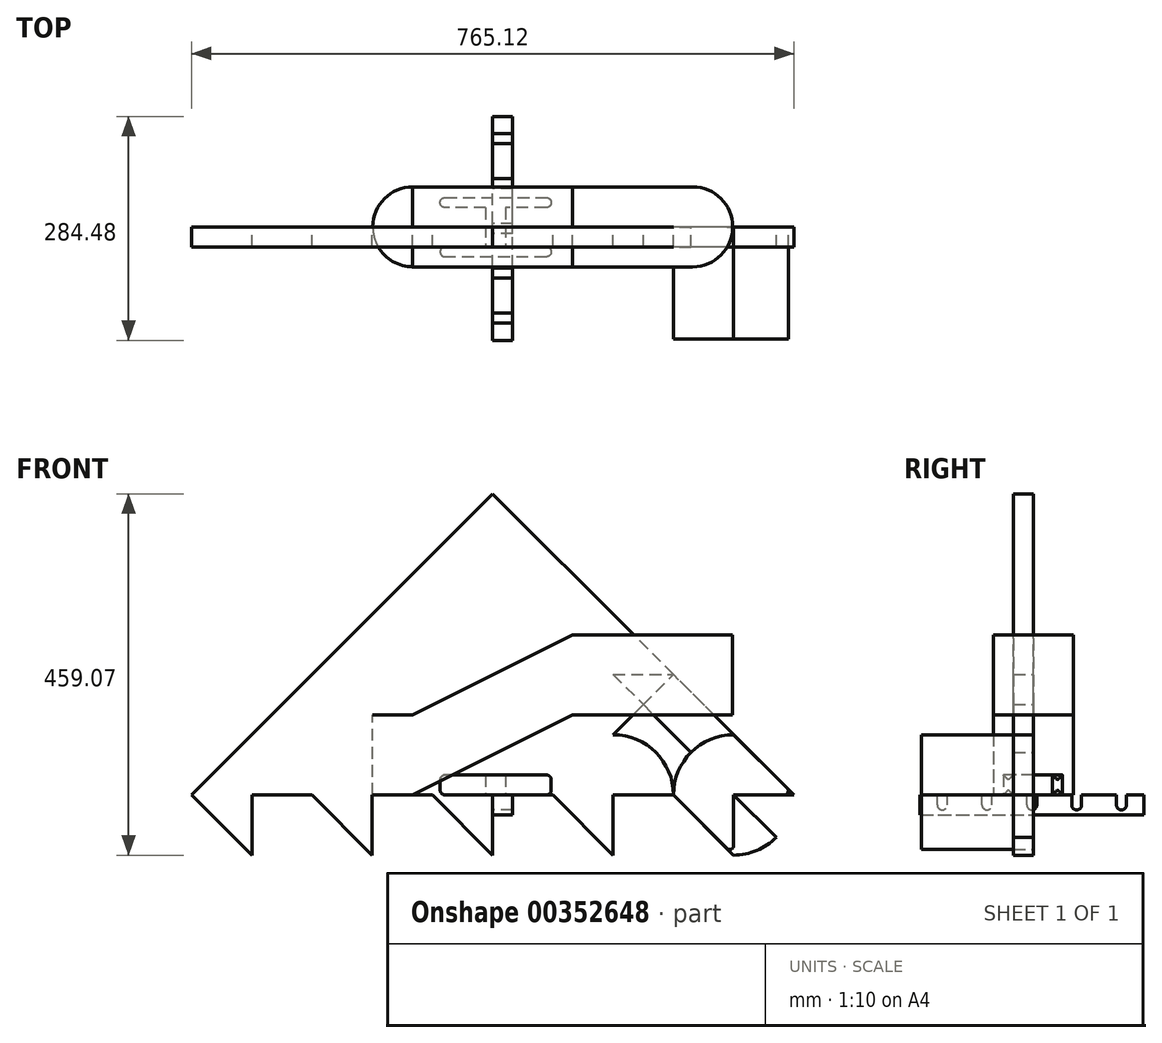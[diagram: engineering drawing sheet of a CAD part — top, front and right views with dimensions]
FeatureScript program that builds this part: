
annotation { "Feature Type Name" : "Feature", "Feature Type Description" : "" }
export const myFeature = defineFeature(function(context is Context, id is Id, definition is map)
    precondition{}
    {
        {
            var Q0;
            Q0=qCreatedBy(makeId("Front.planeOp"),FACE);
            var sketch = newSketch(context, id + "F0", { "sketchPlane" : qUnion([Q0])});
            skPoint(sketch, "E0", {"position": v(-101.6, 0) * mm});
            skPoint(sketch, "E1", {"position": v(101.6, 101.6) * mm});
            skLineSegment(sketch, "E2", {"start": v(-101.6, 0) * mm, "end": v(101.6, 0) * mm});
            skLineSegment(sketch, "E3", {"start": v(101.6, 0) * mm, "end": v(101.6, 101.6) * mm});
            skLineSegment(sketch, "E4", {"start": v(101.6, 101.6) * mm, "end": v(-101.6, 101.6) * mm});
            skLineSegment(sketch, "E5", {"start": v(-101.6, 101.6) * mm, "end": v(-101.6, 0) * mm});
            skLineSegment(sketch, "E6", {"start": v(-101.6, 203.2) * mm, "end": v(-101.6, 101.6) * mm});
            skLineSegment(sketch, "E7", {"start": v(101.6, 203.2) * mm, "end": v(101.6, 101.6) * mm});
            skLineSegment(sketch, "E8", {"start": v(-101.6, 203.2) * mm, "end": v(-101.6, 203.2) * mm});
            skLineSegment(sketch, "E9", {"start": v(101.6, 203.2) * mm, "end": v(101.6, 203.2) * mm});
            skLineSegment(sketch, "E10", {"start": v(101.6, 152.4) * mm, "end": v(-101.6, 152.4) * mm});
            skLineSegment(sketch, "E11", {"start": v(101.6, 50.8) * mm, "end": v(-101.6, 50.8) * mm});
            skLineSegment(sketch, "E12", {"start": v(101.6, 203.2) * mm, "end": v(-101.6, 203.2) * mm});
            skLineSegment(sketch, "E13", {"start": v(0, 203.2) * mm, "end": v(0, 0) * mm});
            skLineSegment(sketch, "E14", {"start": v(101.6, 203.2) * mm, "end": v(-101.6, 101.6) * mm});
            skLineSegment(sketch, "E15", {"start": v(101.6, 101.6) * mm, "end": v(-101.6, 0) * mm});
            skLineSegment(sketch, "E16.0", {"start": v(203.2, 0) * mm, "end": v(203.2, 101.6) * mm});
            skLineSegment(sketch, "E16.1", {"start": v(203.2, 203.2) * mm, "end": v(203.2, 101.6) * mm});
            skLineSegment(sketch, "E17.0", {"start": v(-203.2, 101.6) * mm, "end": v(-203.2, 0) * mm});
            skLineSegment(sketch, "E17.1", {"start": v(-203.2, 203.2) * mm, "end": v(-203.2, 101.6) * mm});
            skLineSegment(sketch, "E18", {"start": v(101.6, 203.2) * mm, "end": v(203.2, 203.2) * mm});
            skLineSegment(sketch, "E19", {"start": v(-101.6, 203.2) * mm, "end": v(-203.2, 203.2) * mm});
            skLineSegment(sketch, "E20", {"start": v(-203.2, 0) * mm, "end": v(-101.6, 0) * mm});
            skLineSegment(sketch, "E21", {"start": v(101.6, 0) * mm, "end": v(203.2, 0) * mm});
            skLineSegment(sketch, "E22", {"start": v(101.6, 101.6) * mm, "end": v(203.2, 101.6) * mm});
            skLineSegment(sketch, "E23", {"start": v(-101.6, 101.6) * mm, "end": v(-203.2, 101.6) * mm});
            skLineSegment(sketch, "E24", {"start": v(152.4, 203.2) * mm, "end": v(152.4, 101.6) * mm});
            skLineSegment(sketch, "E25", {"start": v(-152.4, 101.6) * mm, "end": v(-152.4, 0) * mm});
            skLineSegment(sketch, "E26.MirrorCS", {"start": v(254, 203.2) * mm, "end": v(254, 101.6) * mm});
            skLineSegment(sketch, "E27.MirrorCS", {"start": v(304.8, 203.2) * mm, "end": v(304.8, 101.6) * mm});
            skLineSegment(sketch, "E28", {"start": v(203.2, 203.2) * mm, "end": v(304.8, 203.2) * mm});
            skLineSegment(sketch, "E29", {"start": v(304.8, 101.6) * mm, "end": v(203.2, 101.6) * mm});
            skLineSegment(sketch, "E30.bottom", {"start": v(-152.4, 101.6) * mm, "end": v(-101.6, 101.6) * mm});
            skLineSegment(sketch, "E30.top", {"start": v(-152.4, 0) * mm, "end": v(-101.6, 0) * mm});
            skLineSegment(sketch, "E31", {"start": v(-108.75, 101.6) * mm, "end": v(-108.75, 0) * mm});
            skSolve(sketch);
        }
        {
            var Q0;
            {var subQ1=sQuery(id+"F0.wireOp",EDGE,"E7");var subQ3=sQuery(id+"F0.wireOp",EDGE,"E10");var subQ4=makeQuery(id+"F0.imprint","INTERSECT",VERTEX,{"derivedFrom":[subQ1,subQ3]});Q0=makeQuery(id+"F0.imprint","IMPRINT",FACE,{"disambiguationData":[TD([[makeQuery(id+"F0.imprint","IMPRINT",EDGE,{"disambiguationData":[TD([[subQ4,-1.0]])],"derivedFrom":subQ3}),-1.0]])]});}
            var Q1;
            {var subQ0=sQuery(id+"F0.wireOp",EDGE,"E7");var subQ5=sQuery(id+"F0.wireOp",EDGE,"E10");var subQ7=makeQuery(id+"F0.imprint","INTERSECT",VERTEX,{"derivedFrom":[subQ0,subQ5]});Q1=makeQuery(id+"F0.imprint","IMPRINT",FACE,{"disambiguationData":[TD([[makeQuery(id+"F0.imprint","IMPRINT",EDGE,{"disambiguationData":[TD([[subQ7,-1.0]])],"derivedFrom":subQ5}),1.0]])]});}
            var Q2;
            {var subQ1=sQuery(id+"F0.wireOp",EDGE,"E4");var subQ3=sQuery(id+"F0.wireOp",EDGE,"E13");var subQ4=makeQuery(id+"F0.imprint","INTERSECT",VERTEX,{"derivedFrom":[subQ1,subQ3]});Q2=makeQuery(id+"F0.imprint","IMPRINT",FACE,{"disambiguationData":[TD([[makeQuery(id+"F0.imprint","IMPRINT",EDGE,{"disambiguationData":[TD([[subQ4,1.0]])],"derivedFrom":subQ3}),-1.0]])]});}
            var Q3;
            {var subQ0=sQuery(id+"F0.wireOp",EDGE,"E5");var subQ5=sQuery(id+"F0.wireOp",EDGE,"E11");var subQ6=makeQuery(id+"F0.imprint","INTERSECT",VERTEX,{"derivedFrom":[subQ0,subQ5]});Q3=makeQuery(id+"F0.imprint","IMPRINT",FACE,{"disambiguationData":[TD([[makeQuery(id+"F0.imprint","IMPRINT",EDGE,{"disambiguationData":[TD([[subQ6,1.0]])],"derivedFrom":subQ5}),-1.0]])]});}
            var Q4;
            {var subQ1=sQuery(id+"F0.wireOp",EDGE,"E4");var subQ3=sQuery(id+"F0.wireOp",EDGE,"E13");var subQ4=makeQuery(id+"F0.imprint","INTERSECT",VERTEX,{"derivedFrom":[subQ1,subQ3]});Q4=makeQuery(id+"F0.imprint","IMPRINT",FACE,{"disambiguationData":[TD([[makeQuery(id+"F0.imprint","IMPRINT",EDGE,{"disambiguationData":[TD([[subQ4,-1.0]])],"derivedFrom":subQ3}),1.0]])]});}
            var Q5;
            {var subQ1=sQuery(id+"F0.wireOp",EDGE,"E5");var subQ3=sQuery(id+"F0.wireOp",EDGE,"E11");var subQ4=makeQuery(id+"F0.imprint","INTERSECT",VERTEX,{"derivedFrom":[subQ1,subQ3]});Q5=makeQuery(id+"F0.imprint","IMPRINT",FACE,{"disambiguationData":[TD([[makeQuery(id+"F0.imprint","IMPRINT",EDGE,{"disambiguationData":[TD([[subQ4,1.0]])],"derivedFrom":subQ3}),1.0]])]});}
            var Q6;
            {var subQ3=sQuery(id+"F0.wireOp",EDGE,"E24");Q6=makeQuery(id+"F0.imprint","IMPRINT",FACE,{"disambiguationData":[TD([[makeQuery(id+"F0.imprint","IMPRINT",EDGE,{"derivedFrom":subQ3}),-1.0]])]});}
            var Q7;
            {var subQ0=sQuery(id+"F0.wireOp",EDGE,"E16.1");Q7=makeQuery(id+"F0.imprint","IMPRINT",FACE,{"disambiguationData":[TD([[makeQuery(id+"F0.imprint","IMPRINT",EDGE,{"derivedFrom":subQ0}),-1.0]])]});}
            var Q8;
            {var subQ0=sQuery(id+"F0.wireOp",EDGE,"E16.1");Q8=makeQuery(id+"F0.imprint","IMPRINT",FACE,{"disambiguationData":[TD([[makeQuery(id+"F0.imprint","IMPRINT",EDGE,{"derivedFrom":subQ0}),1.0]])]});}
            extrude(context, id + "F1", {"entities" : qUnion([Q0, Q1, Q2, Q3, Q4, Q5, Q6, Q7, Q8]), "endBound" : BoundingType.SYMMETRIC, "depth" : 101.6 * mm});
        }
        {
            var Q0;
            {var subQ0=sQuery(id+"F0.wireOp",EDGE,"E26.MirrorCS");Q0=makeQuery(id+"F0.imprint","IMPRINT",FACE,{"disambiguationData":[TD([[makeQuery(id+"F0.imprint","IMPRINT",EDGE,{"derivedFrom":subQ0}),1.0]])]});}
            var Q1;
            Q1=sQuery(id+"F0.wireOp",EDGE,"E26.MirrorCS");
            revolve(context, id + "F2", {"operationType" : NewBodyOperationType.ADD, "entities" : qUnion([Q0]), "axis" : qUnion([Q1]), "revolveType" : RevolveType.SYMMETRIC, "angle" : 180 * degree});
        }
        {
            var Q0;
            {var subQ6=sQuery(id+"F0.wireOp",EDGE,"E31");Q0=makeQuery(id+"F0.imprint","IMPRINT",FACE,{"disambiguationData":[TD([[makeQuery(id+"F0.imprint","IMPRINT",EDGE,{"derivedFrom":subQ6}),1.0]])]});}
            extrude(context, id + "F3", {"entities" : qUnion([Q0]), "operationType" : NewBodyOperationType.ADD, "depth" : 2.3 * mm});
        }
        {
            var Q0;
            {var subQ0=sQuery(id+"F0.wireOp",EDGE,"E25");Q0=makeQuery(id+"F0.imprint","IMPRINT",FACE,{"disambiguationData":[TD([[makeQuery(id+"F0.imprint","IMPRINT",EDGE,{"derivedFrom":subQ0}),1.0]])]});}
            var Q1;
            {var subQ6=sQuery(id+"F0.wireOp",EDGE,"E31");Q1=makeQuery(id+"F0.imprint","IMPRINT",FACE,{"disambiguationData":[TD([[makeQuery(id+"F0.imprint","IMPRINT",EDGE,{"derivedFrom":subQ6}),1.0]])]});}
            var Q2;
            Q2=makeQuery(id+"F3.opExtrude","CAP_EDGE",EDGE,{"disambiguationData":[OSD([sQuery(id+"F0.wireOp",EDGE,"E5")])],"isStart":true});
            revolve(context, id + "F4", {"operationType" : NewBodyOperationType.ADD, "entities" : qUnion([Q0, Q1]), "axis" : qUnion([Q2]), "revolveType" : RevolveType.SYMMETRIC, "angle" : 180 * degree});
        }
        {
            var Q0;
            Q0=qCreatedBy(makeId("Right.planeOp"),FACE);
            var sketch = newSketch(context, id + "F5", { "sketchPlane" : qUnion([Q0])});
            skLineSegment(sketch, "E32.bottom", {"start": v(-144.13, 0) * mm, "end": v(140.35, 0) * mm});
            skLineSegment(sketch, "E32.top", {"start": v(-144.13, -25.4) * mm, "end": v(140.35, -25.4) * mm});
            skLineSegment(sketch, "E32.left", {"start": v(-144.13, 0) * mm, "end": v(-144.13, -25.4) * mm});
            skLineSegment(sketch, "E32.right", {"start": v(140.35, 0) * mm, "end": v(140.35, -25.4) * mm});
            skLineSegment(sketch, "E33", {"start": v(-144.13, -12.7) * mm, "end": v(140.35, -12.7) * mm});
            skLineSegment(sketch, "E34.0", {"start": v(-144.13, -6.35) * mm, "end": v(140.35, -6.35) * mm});
            skLineSegment(sketch, "E35.0", {"start": v(-87.23, 0) * mm, "end": v(-87.23, -25.4) * mm});
            skLineSegment(sketch, "E36.0", {"start": v(-30.34, 0) * mm, "end": v(-30.34, -25.4) * mm});
            skLineSegment(sketch, "E37.0", {"start": v(26.56, 0) * mm, "end": v(26.56, -25.4) * mm});
            skLineSegment(sketch, "E38.0", {"start": v(83.45, 0) * mm, "end": v(83.45, -25.4) * mm});
            skLineSegment(sketch, "E39.0", {"start": v(-115.68, 0) * mm, "end": v(-115.68, -25.4) * mm});
            skLineSegment(sketch, "E40.0", {"start": v(-58.79, 0) * mm, "end": v(-58.79, -25.4) * mm});
            skLineSegment(sketch, "E41.0", {"start": v(-1.89, 0) * mm, "end": v(-1.89, -25.4) * mm});
            skLineSegment(sketch, "E42.0", {"start": v(55, 0) * mm, "end": v(55, -25.4) * mm});
            skLineSegment(sketch, "E43.0", {"start": v(111.9, 0) * mm, "end": v(111.9, -25.4) * mm});
            skCircle(sketch, "E44", {"center": v(-115.68, -12.7) * mm, "radius": 6.35 * mm});
            skCircle(sketch, "E45", {"center": v(-58.79, -12.7) * mm, "radius": 6.35 * mm});
            skCircle(sketch, "E46", {"center": v(-1.89, -12.7) * mm, "radius": 6.35 * mm});
            skCircle(sketch, "E47", {"center": v(55, -12.7) * mm, "radius": 6.35 * mm});
            skCircle(sketch, "E48", {"center": v(111.9, -12.7) * mm, "radius": 6.35 * mm});
            skLineSegment(sketch, "E49", {"start": v(-109.33, -12.7) * mm, "end": v(-109.33, 0) * mm});
            skLineSegment(sketch, "E50", {"start": v(-122.03, -12.7) * mm, "end": v(-122.03, 0) * mm});
            skLineSegment(sketch, "E51", {"start": v(-65.14, -12.7) * mm, "end": v(-65.14, 0) * mm});
            skLineSegment(sketch, "E52", {"start": v(-52.44, -12.7) * mm, "end": v(-52.44, 0) * mm});
            skLineSegment(sketch, "E53", {"start": v(-8.24, -12.7) * mm, "end": v(-8.24, 0) * mm});
            skLineSegment(sketch, "E54", {"start": v(4.46, -12.7) * mm, "end": v(4.46, 0) * mm});
            skLineSegment(sketch, "E55", {"start": v(61.36, -12.7) * mm, "end": v(61.36, 0) * mm});
            skLineSegment(sketch, "E56", {"start": v(48.66, -12.7) * mm, "end": v(48.66, 0) * mm});
            skLineSegment(sketch, "E57", {"start": v(118.25, -12.7) * mm, "end": v(118.25, 0) * mm});
            skLineSegment(sketch, "E58", {"start": v(105.55, -12.7) * mm, "end": v(105.55, 0) * mm});
            skSolve(sketch);
        }
        {
            var Q0;
            {var subQ0=sQuery(id+"F5.wireOp",EDGE,"E32.left");var subQ1=sQuery(id+"F5.wireOp",EDGE,"E32.bottom");var subQ2=makeQuery(id+"F5.imprint","INTERSECT",VERTEX,{"derivedFrom":[subQ1,subQ0]});Q0=makeQuery(id+"F5.imprint","IMPRINT",FACE,{"disambiguationData":[TD([[makeQuery(id+"F5.imprint","IMPRINT",EDGE,{"disambiguationData":[TD([[subQ2,-1.0]])],"derivedFrom":subQ1}),-1.0]])]});}
            var Q1;
            {var subQ0=sQuery(id+"F5.wireOp",EDGE,"E32.right");var subQ1=sQuery(id+"F5.wireOp",EDGE,"E32.bottom");var subQ2=makeQuery(id+"F5.imprint","INTERSECT",VERTEX,{"derivedFrom":[subQ1,subQ0]});Q1=makeQuery(id+"F5.imprint","IMPRINT",FACE,{"disambiguationData":[TD([[makeQuery(id+"F5.imprint","IMPRINT",EDGE,{"disambiguationData":[TD([[subQ2,1.0]])],"derivedFrom":subQ1}),-1.0]])]});}
            var Q2;
            {var subQ0=sQuery(id+"F5.wireOp",EDGE,"E35.0");var subQ1=sQuery(id+"F5.wireOp",EDGE,"E32.bottom");var subQ2=makeQuery(id+"F5.imprint","INTERSECT",VERTEX,{"derivedFrom":[subQ1,subQ0]});Q2=makeQuery(id+"F5.imprint","IMPRINT",FACE,{"disambiguationData":[TD([[makeQuery(id+"F5.imprint","IMPRINT",EDGE,{"disambiguationData":[TD([[subQ2,-1.0]])],"derivedFrom":subQ1}),-1.0]])]});}
            var Q3;
            {var subQ0=sQuery(id+"F5.wireOp",EDGE,"E36.0");var subQ1=sQuery(id+"F5.wireOp",EDGE,"E32.bottom");var subQ2=makeQuery(id+"F5.imprint","INTERSECT",VERTEX,{"derivedFrom":[subQ1,subQ0]});Q3=makeQuery(id+"F5.imprint","IMPRINT",FACE,{"disambiguationData":[TD([[makeQuery(id+"F5.imprint","IMPRINT",EDGE,{"disambiguationData":[TD([[subQ2,1.0]])],"derivedFrom":subQ1}),-1.0]])]});}
            var Q4;
            {var subQ0=sQuery(id+"F5.wireOp",EDGE,"E36.0");var subQ1=sQuery(id+"F5.wireOp",EDGE,"E32.bottom");var subQ2=makeQuery(id+"F5.imprint","INTERSECT",VERTEX,{"derivedFrom":[subQ1,subQ0]});Q4=makeQuery(id+"F5.imprint","IMPRINT",FACE,{"disambiguationData":[TD([[makeQuery(id+"F5.imprint","IMPRINT",EDGE,{"disambiguationData":[TD([[subQ2,-1.0]])],"derivedFrom":subQ1}),-1.0]])]});}
            var Q5;
            {var subQ0=sQuery(id+"F5.wireOp",EDGE,"E37.0");var subQ1=sQuery(id+"F5.wireOp",EDGE,"E32.bottom");var subQ2=makeQuery(id+"F5.imprint","INTERSECT",VERTEX,{"derivedFrom":[subQ1,subQ0]});Q5=makeQuery(id+"F5.imprint","IMPRINT",FACE,{"disambiguationData":[TD([[makeQuery(id+"F5.imprint","IMPRINT",EDGE,{"disambiguationData":[TD([[subQ2,1.0]])],"derivedFrom":subQ1}),-1.0]])]});}
            var Q6;
            {var subQ0=sQuery(id+"F5.wireOp",EDGE,"E37.0");var subQ1=sQuery(id+"F5.wireOp",EDGE,"E32.bottom");var subQ2=makeQuery(id+"F5.imprint","INTERSECT",VERTEX,{"derivedFrom":[subQ1,subQ0]});Q6=makeQuery(id+"F5.imprint","IMPRINT",FACE,{"disambiguationData":[TD([[makeQuery(id+"F5.imprint","IMPRINT",EDGE,{"disambiguationData":[TD([[subQ2,-1.0]])],"derivedFrom":subQ1}),-1.0]])]});}
            var Q7;
            {var subQ0=sQuery(id+"F5.wireOp",EDGE,"E38.0");var subQ1=sQuery(id+"F5.wireOp",EDGE,"E32.bottom");var subQ2=makeQuery(id+"F5.imprint","INTERSECT",VERTEX,{"derivedFrom":[subQ1,subQ0]});Q7=makeQuery(id+"F5.imprint","IMPRINT",FACE,{"disambiguationData":[TD([[makeQuery(id+"F5.imprint","IMPRINT",EDGE,{"disambiguationData":[TD([[subQ2,1.0]])],"derivedFrom":subQ1}),-1.0]])]});}
            var Q8;
            {var subQ0=sQuery(id+"F5.wireOp",EDGE,"E38.0");var subQ1=sQuery(id+"F5.wireOp",EDGE,"E32.bottom");var subQ2=makeQuery(id+"F5.imprint","INTERSECT",VERTEX,{"derivedFrom":[subQ1,subQ0]});Q8=makeQuery(id+"F5.imprint","IMPRINT",FACE,{"disambiguationData":[TD([[makeQuery(id+"F5.imprint","IMPRINT",EDGE,{"disambiguationData":[TD([[subQ2,-1.0]])],"derivedFrom":subQ1}),-1.0]])]});}
            var Q9;
            {var subQ1=sQuery(id+"F5.wireOp",EDGE,"E32.top");var subQ6=sQuery(id+"F5.wireOp",EDGE,"E32.left");var subQ9=makeQuery(id+"F5.imprint","INTERSECT",VERTEX,{"derivedFrom":[subQ1,subQ6]});Q9=makeQuery(id+"F5.imprint","IMPRINT",FACE,{"disambiguationData":[TD([[makeQuery(id+"F5.imprint","IMPRINT",EDGE,{"disambiguationData":[TD([[subQ9,-1.0]])],"derivedFrom":subQ1}),1.0]])]});}
            var Q10;
            {var subQ1=sQuery(id+"F5.wireOp",EDGE,"E32.top");var subQ6=sQuery(id+"F5.wireOp",EDGE,"E32.right");var subQ9=makeQuery(id+"F5.imprint","INTERSECT",VERTEX,{"derivedFrom":[subQ1,subQ6]});Q10=makeQuery(id+"F5.imprint","IMPRINT",FACE,{"disambiguationData":[TD([[makeQuery(id+"F5.imprint","IMPRINT",EDGE,{"disambiguationData":[TD([[subQ9,1.0]])],"derivedFrom":subQ1}),1.0]])]});}
            var Q11;
            {var subQ0=sQuery(id+"F5.wireOp",EDGE,"E33");var subQ1=sQuery(id+"F5.wireOp",EDGE,"E32.left");var subQ2=makeQuery(id+"F5.imprint","INTERSECT",VERTEX,{"derivedFrom":[subQ1,subQ0]});Q11=makeQuery(id+"F5.imprint","IMPRINT",FACE,{"disambiguationData":[TD([[makeQuery(id+"F5.imprint","IMPRINT",EDGE,{"disambiguationData":[TD([[subQ2,1.0]])],"derivedFrom":subQ1}),1.0]])]});}
            var Q12;
            {var subQ0=sQuery(id+"F5.wireOp",EDGE,"E35.0");var subQ1=sQuery(id+"F5.wireOp",EDGE,"E32.top");var subQ2=makeQuery(id+"F5.imprint","INTERSECT",VERTEX,{"derivedFrom":[subQ1,subQ0]});Q12=makeQuery(id+"F5.imprint","IMPRINT",FACE,{"disambiguationData":[TD([[makeQuery(id+"F5.imprint","IMPRINT",EDGE,{"disambiguationData":[TD([[subQ2,1.0]])],"derivedFrom":subQ1}),1.0]])]});}
            var Q13;
            {var subQ0=sQuery(id+"F5.wireOp",EDGE,"E35.0");var subQ1=sQuery(id+"F5.wireOp",EDGE,"E32.top");var subQ2=makeQuery(id+"F5.imprint","INTERSECT",VERTEX,{"derivedFrom":[subQ1,subQ0]});Q13=makeQuery(id+"F5.imprint","IMPRINT",FACE,{"disambiguationData":[TD([[makeQuery(id+"F5.imprint","IMPRINT",EDGE,{"disambiguationData":[TD([[subQ2,-1.0]])],"derivedFrom":subQ1}),1.0]])]});}
            var Q14;
            {var subQ1=sQuery(id+"F5.wireOp",EDGE,"E32.top");var subQ5=sQuery(id+"F5.wireOp",EDGE,"E36.0");var subQ6=makeQuery(id+"F5.imprint","INTERSECT",VERTEX,{"derivedFrom":[subQ1,subQ5]});Q14=makeQuery(id+"F5.imprint","IMPRINT",FACE,{"disambiguationData":[TD([[makeQuery(id+"F5.imprint","IMPRINT",EDGE,{"disambiguationData":[TD([[subQ6,1.0]])],"derivedFrom":subQ1}),1.0]])]});}
            var Q15;
            {var subQ0=sQuery(id+"F5.wireOp",EDGE,"E36.0");var subQ1=sQuery(id+"F5.wireOp",EDGE,"E32.top");var subQ2=makeQuery(id+"F5.imprint","INTERSECT",VERTEX,{"derivedFrom":[subQ1,subQ0]});Q15=makeQuery(id+"F5.imprint","IMPRINT",FACE,{"disambiguationData":[TD([[makeQuery(id+"F5.imprint","IMPRINT",EDGE,{"disambiguationData":[TD([[subQ2,-1.0]])],"derivedFrom":subQ1}),1.0]])]});}
            var Q16;
            {var subQ1=sQuery(id+"F5.wireOp",EDGE,"E32.top");var subQ5=sQuery(id+"F5.wireOp",EDGE,"E37.0");var subQ6=makeQuery(id+"F5.imprint","INTERSECT",VERTEX,{"derivedFrom":[subQ1,subQ5]});Q16=makeQuery(id+"F5.imprint","IMPRINT",FACE,{"disambiguationData":[TD([[makeQuery(id+"F5.imprint","IMPRINT",EDGE,{"disambiguationData":[TD([[subQ6,1.0]])],"derivedFrom":subQ1}),1.0]])]});}
            var Q17;
            {var subQ0=sQuery(id+"F5.wireOp",EDGE,"E37.0");var subQ1=sQuery(id+"F5.wireOp",EDGE,"E32.top");var subQ2=makeQuery(id+"F5.imprint","INTERSECT",VERTEX,{"derivedFrom":[subQ1,subQ0]});Q17=makeQuery(id+"F5.imprint","IMPRINT",FACE,{"disambiguationData":[TD([[makeQuery(id+"F5.imprint","IMPRINT",EDGE,{"disambiguationData":[TD([[subQ2,-1.0]])],"derivedFrom":subQ1}),1.0]])]});}
            var Q18;
            {var subQ1=sQuery(id+"F5.wireOp",EDGE,"E32.top");var subQ7=sQuery(id+"F5.wireOp",EDGE,"E38.0");var subQ9=makeQuery(id+"F5.imprint","INTERSECT",VERTEX,{"derivedFrom":[subQ1,subQ7]});Q18=makeQuery(id+"F5.imprint","IMPRINT",FACE,{"disambiguationData":[TD([[makeQuery(id+"F5.imprint","IMPRINT",EDGE,{"disambiguationData":[TD([[subQ9,1.0]])],"derivedFrom":subQ1}),1.0]])]});}
            var Q19;
            {var subQ1=sQuery(id+"F5.wireOp",EDGE,"E32.top");var subQ7=sQuery(id+"F5.wireOp",EDGE,"E38.0");var subQ9=makeQuery(id+"F5.imprint","INTERSECT",VERTEX,{"derivedFrom":[subQ1,subQ7]});Q19=makeQuery(id+"F5.imprint","IMPRINT",FACE,{"disambiguationData":[TD([[makeQuery(id+"F5.imprint","IMPRINT",EDGE,{"disambiguationData":[TD([[subQ9,-1.0]])],"derivedFrom":subQ1}),1.0]])]});}
            var Q20;
            {var subQ0=sQuery(id+"F5.wireOp",EDGE,"E49");var subQ5=sQuery(id+"F5.wireOp",EDGE,"E34.0");var subQ6=makeQuery(id+"F5.imprint","INTERSECT",VERTEX,{"derivedFrom":[subQ5,subQ0]});Q20=makeQuery(id+"F5.imprint","IMPRINT",FACE,{"disambiguationData":[TD([[makeQuery(id+"F5.imprint","IMPRINT",EDGE,{"disambiguationData":[TD([[subQ6,-1.0]])],"derivedFrom":subQ5}),-1.0]])]});}
            var Q21;
            {var subQ0=sQuery(id+"F5.wireOp",EDGE,"E35.0");var subQ1=sQuery(id+"F5.wireOp",EDGE,"E32.bottom");var subQ2=makeQuery(id+"F5.imprint","INTERSECT",VERTEX,{"derivedFrom":[subQ1,subQ0]});Q21=makeQuery(id+"F5.imprint","IMPRINT",FACE,{"disambiguationData":[TD([[makeQuery(id+"F5.imprint","IMPRINT",EDGE,{"disambiguationData":[TD([[subQ2,1.0]])],"derivedFrom":subQ1}),-1.0]])]});}
            var Q22;
            {var subQ3=sQuery(id+"F5.wireOp",EDGE,"E35.0");var subQ5=sQuery(id+"F5.wireOp",EDGE,"E34.0");var subQ6=makeQuery(id+"F5.imprint","INTERSECT",VERTEX,{"derivedFrom":[subQ5,subQ3]});Q22=makeQuery(id+"F5.imprint","IMPRINT",FACE,{"disambiguationData":[TD([[makeQuery(id+"F5.imprint","IMPRINT",EDGE,{"disambiguationData":[TD([[subQ6,-1.0]])],"derivedFrom":subQ5}),-1.0]])]});}
            var Q23;
            {var subQ0=sQuery(id+"F5.wireOp",EDGE,"E52");var subQ5=sQuery(id+"F5.wireOp",EDGE,"E34.0");var subQ6=makeQuery(id+"F5.imprint","INTERSECT",VERTEX,{"derivedFrom":[subQ5,subQ0]});Q23=makeQuery(id+"F5.imprint","IMPRINT",FACE,{"disambiguationData":[TD([[makeQuery(id+"F5.imprint","IMPRINT",EDGE,{"disambiguationData":[TD([[subQ6,-1.0]])],"derivedFrom":subQ5}),-1.0]])]});}
            var Q24;
            {var subQ3=sQuery(id+"F5.wireOp",EDGE,"E36.0");var subQ5=sQuery(id+"F5.wireOp",EDGE,"E34.0");var subQ6=makeQuery(id+"F5.imprint","INTERSECT",VERTEX,{"derivedFrom":[subQ5,subQ3]});Q24=makeQuery(id+"F5.imprint","IMPRINT",FACE,{"disambiguationData":[TD([[makeQuery(id+"F5.imprint","IMPRINT",EDGE,{"disambiguationData":[TD([[subQ6,-1.0]])],"derivedFrom":subQ5}),-1.0]])]});}
            var Q25;
            {var subQ0=sQuery(id+"F5.wireOp",EDGE,"E54");var subQ5=sQuery(id+"F5.wireOp",EDGE,"E34.0");var subQ6=makeQuery(id+"F5.imprint","INTERSECT",VERTEX,{"derivedFrom":[subQ5,subQ0]});Q25=makeQuery(id+"F5.imprint","IMPRINT",FACE,{"disambiguationData":[TD([[makeQuery(id+"F5.imprint","IMPRINT",EDGE,{"disambiguationData":[TD([[subQ6,-1.0]])],"derivedFrom":subQ5}),-1.0]])]});}
            var Q26;
            {var subQ3=sQuery(id+"F5.wireOp",EDGE,"E37.0");var subQ5=sQuery(id+"F5.wireOp",EDGE,"E34.0");var subQ6=makeQuery(id+"F5.imprint","INTERSECT",VERTEX,{"derivedFrom":[subQ5,subQ3]});Q26=makeQuery(id+"F5.imprint","IMPRINT",FACE,{"disambiguationData":[TD([[makeQuery(id+"F5.imprint","IMPRINT",EDGE,{"disambiguationData":[TD([[subQ6,-1.0]])],"derivedFrom":subQ5}),-1.0]])]});}
            var Q27;
            {var subQ0=sQuery(id+"F5.wireOp",EDGE,"E55");var subQ5=sQuery(id+"F5.wireOp",EDGE,"E34.0");var subQ6=makeQuery(id+"F5.imprint","INTERSECT",VERTEX,{"derivedFrom":[subQ5,subQ0]});Q27=makeQuery(id+"F5.imprint","IMPRINT",FACE,{"disambiguationData":[TD([[makeQuery(id+"F5.imprint","IMPRINT",EDGE,{"disambiguationData":[TD([[subQ6,-1.0]])],"derivedFrom":subQ5}),-1.0]])]});}
            var Q28;
            {var subQ3=sQuery(id+"F5.wireOp",EDGE,"E38.0");var subQ5=sQuery(id+"F5.wireOp",EDGE,"E34.0");var subQ6=makeQuery(id+"F5.imprint","INTERSECT",VERTEX,{"derivedFrom":[subQ5,subQ3]});Q28=makeQuery(id+"F5.imprint","IMPRINT",FACE,{"disambiguationData":[TD([[makeQuery(id+"F5.imprint","IMPRINT",EDGE,{"disambiguationData":[TD([[subQ6,-1.0]])],"derivedFrom":subQ5}),-1.0]])]});}
            var Q29;
            {var subQ0=sQuery(id+"F5.wireOp",EDGE,"E33");var subQ1=sQuery(id+"F5.wireOp",EDGE,"E32.right");var subQ2=makeQuery(id+"F5.imprint","INTERSECT",VERTEX,{"derivedFrom":[subQ1,subQ0]});Q29=makeQuery(id+"F5.imprint","IMPRINT",FACE,{"disambiguationData":[TD([[makeQuery(id+"F5.imprint","IMPRINT",EDGE,{"disambiguationData":[TD([[subQ2,1.0]])],"derivedFrom":subQ1}),-1.0]])]});}
            var Q30;
            Q30=sQuery(id+"F5.wireOp",EDGE,"E44");
            var Q31;
            Q31=sQuery(id+"F5.wireOp",EDGE,"E47");
            var Q32;
            Q32=sQuery(id+"F5.wireOp",EDGE,"E39.0");
            var Q33;
            Q33=sQuery(id+"F5.wireOp",EDGE,"E41.0");
            var Q34;
            Q34=sQuery(id+"F5.wireOp",EDGE,"E37.0");
            var Q35;
            Q35=sQuery(id+"F5.wireOp",EDGE,"E45");
            var Q36;
            Q36=sQuery(id+"F5.wireOp",EDGE,"E51");
            var Q37;
            Q37=sQuery(id+"F5.wireOp",EDGE,"E35.0");
            var Q38;
            Q38=sQuery(id+"F5.wireOp",EDGE,"E56");
            var Q39;
            Q39=sQuery(id+"F5.wireOp",EDGE,"E49");
            var Q40;
            Q40=sQuery(id+"F5.wireOp",EDGE,"E40.0");
            var Q41;
            Q41=sQuery(id+"F5.wireOp",EDGE,"E57");
            var Q42;
            Q42=sQuery(id+"F5.wireOp",EDGE,"E46");
            var Q43;
            Q43=sQuery(id+"F5.wireOp",EDGE,"E48");
            var Q44;
            Q44=sQuery(id+"F5.wireOp",EDGE,"E52");
            var Q45;
            Q45=sQuery(id+"F5.wireOp",EDGE,"E54");
            var Q46;
            Q46=sQuery(id+"F5.wireOp",EDGE,"E50");
            var Q47;
            Q47=sQuery(id+"F5.wireOp",EDGE,"E58");
            var Q48;
            Q48=sQuery(id+"F5.wireOp",EDGE,"E36.0");
            var Q49;
            Q49=sQuery(id+"F5.wireOp",EDGE,"E53");
            var Q50;
            Q50=sQuery(id+"F5.wireOp",EDGE,"E43.0");
            var Q51;
            Q51=sQuery(id+"F5.wireOp",EDGE,"E42.0");
            var Q52;
            Q52=sQuery(id+"F5.wireOp",EDGE,"E55");
            var Q53;
            Q53=sQuery(id+"F5.wireOp",EDGE,"E38.0");
            var Q54;
            Q54=sQuery(id+"F5.wireOp",EDGE,"E32.top");
            var Q55;
            Q55=sQuery(id+"F5.wireOp",EDGE,"E34.0");
            var Q56;
            Q56=sQuery(id+"F5.wireOp",EDGE,"E33");
            var Q57;
            Q57=sQuery(id+"F5.wireOp",EDGE,"E32.bottom");
            extrude(context, id + "F6", {"entities" : qUnion([Q0, Q1, Q2, Q3, Q4, Q5, Q6, Q7, Q8, Q9, Q10, Q11, Q12, Q13, Q14, Q15, Q16, Q17, Q18, Q19, Q20, Q21, Q22, Q23, Q24, Q25, Q26, Q27, Q28, Q29]), "surfaceEntities" : qUnion([Q30, Q31, Q32, Q33, Q34, Q35, Q36, Q37, Q38, Q39, Q40, Q41, Q42, Q43, Q44, Q45, Q46, Q47, Q48, Q49, Q50, Q51, Q52, Q53, Q54, Q55, Q56, Q57]), "depth" : 25.4 * mm});
        }
        {
            var Q0;
            Q0=qCreatedBy(makeId("Top.planeOp"),FACE);
            var sketch = newSketch(context, id + "F7", { "sketchPlane" : qUnion([Q0])});
            skLineSegment(sketch, "E59", {"start": v(-66.87, 37.17) * mm, "end": v(74.26, 37.17) * mm});
            skLineSegment(sketch, "E60", {"start": v(74.26, 37.17) * mm, "end": v(74.26, 24.47) * mm});
            skLineSegment(sketch, "E61", {"start": v(74.26, 24.47) * mm, "end": v(-66.87, 24.47) * mm});
            skLineSegment(sketch, "E62", {"start": v(-66.87, 24.47) * mm, "end": v(-66.87, 37.17) * mm});
            skLineSegment(sketch, "E63", {"start": v(3.7, 24.47) * mm, "end": v(3.7, 24.47) * mm});
            skPoint(sketch, "E63.endSnap0", {"position": v(3.7, 24.47) * mm});
            skLineSegment(sketch, "E64", {"start": v(-66.87, 24.47) * mm, "end": v(-66.87, -38.13) * mm});
            skLineSegment(sketch, "E65", {"start": v(74.26, 24.47) * mm, "end": v(74.26, -38.13) * mm});
            skLineSegment(sketch, "E66", {"start": v(74.26, -38.13) * mm, "end": v(-66.87, -38.13) * mm});
            skLineSegment(sketch, "E67", {"start": v(3.7, 37.17) * mm, "end": v(3.7, -38.13) * mm});
            skLineSegment(sketch, "E68", {"start": v(-9, 24.47) * mm, "end": v(-9, -38.13) * mm});
            skLineSegment(sketch, "E69", {"start": v(16.4, 24.47) * mm, "end": v(16.4, -38.13) * mm});
            skLineSegment(sketch, "E70", {"start": v(-66.87, -25.43) * mm, "end": v(74.26, -25.43) * mm});
            skSolve(sketch);
        }
        {
            var Q0;
            {var subQ0=sQuery(id+"F7.wireOp",EDGE,"E66");var subQ1=sQuery(id+"F7.wireOp",EDGE,"E64");var subQ2=makeQuery(id+"F7.imprint","INTERSECT",VERTEX,{"derivedFrom":[subQ1,subQ0]});Q0=makeQuery(id+"F7.imprint","IMPRINT",FACE,{"disambiguationData":[TD([[makeQuery(id+"F7.imprint","IMPRINT",EDGE,{"disambiguationData":[TD([[subQ2,1.0]])],"derivedFrom":subQ1}),1.0]])]});}
            var Q1;
            {var subQ0=sQuery(id+"F7.wireOp",EDGE,"E66");var subQ1=sQuery(id+"F7.wireOp",EDGE,"E65");var subQ2=makeQuery(id+"F7.imprint","INTERSECT",VERTEX,{"derivedFrom":[subQ1,subQ0]});Q1=makeQuery(id+"F7.imprint","IMPRINT",FACE,{"disambiguationData":[TD([[makeQuery(id+"F7.imprint","IMPRINT",EDGE,{"disambiguationData":[TD([[subQ2,1.0]])],"derivedFrom":subQ1}),-1.0]])]});}
            var Q2;
            {var subQ0=sQuery(id+"F7.wireOp",EDGE,"E62");Q2=makeQuery(id+"F7.imprint","IMPRINT",FACE,{"disambiguationData":[TD([[makeQuery(id+"F7.imprint","IMPRINT",EDGE,{"derivedFrom":subQ0}),-1.0]])]});}
            var Q3;
            {var subQ4=sQuery(id+"F7.wireOp",EDGE,"E60");Q3=makeQuery(id+"F7.imprint","IMPRINT",FACE,{"disambiguationData":[TD([[makeQuery(id+"F7.imprint","IMPRINT",EDGE,{"derivedFrom":subQ4}),-1.0]])]});}
            var Q4;
            {var subQ0=sQuery(id+"F7.wireOp",EDGE,"E67");var subQ1=sQuery(id+"F7.wireOp",EDGE,"E66");var subQ2=makeQuery(id+"F7.imprint","INTERSECT",VERTEX,{"derivedFrom":[subQ1,subQ0]});Q4=makeQuery(id+"F7.imprint","IMPRINT",FACE,{"disambiguationData":[TD([[makeQuery(id+"F7.imprint","IMPRINT",EDGE,{"disambiguationData":[TD([[subQ2,1.0]])],"derivedFrom":subQ1}),-1.0]])]});}
            var Q5;
            {var subQ0=sQuery(id+"F7.wireOp",EDGE,"E67");var subQ1=sQuery(id+"F7.wireOp",EDGE,"E66");var subQ2=makeQuery(id+"F7.imprint","INTERSECT",VERTEX,{"derivedFrom":[subQ1,subQ0]});Q5=makeQuery(id+"F7.imprint","IMPRINT",FACE,{"disambiguationData":[TD([[makeQuery(id+"F7.imprint","IMPRINT",EDGE,{"disambiguationData":[TD([[subQ2,-1.0]])],"derivedFrom":subQ1}),-1.0]])]});}
            var Q6;
            {var subQ0=sQuery(id+"F7.wireOp",EDGE,"E68");var subQ1=sQuery(id+"F7.wireOp",EDGE,"E61");var subQ2=makeQuery(id+"F7.imprint","INTERSECT",VERTEX,{"derivedFrom":[subQ1,subQ0]});Q6=makeQuery(id+"F7.imprint","IMPRINT",FACE,{"disambiguationData":[TD([[makeQuery(id+"F7.imprint","IMPRINT",EDGE,{"disambiguationData":[TD([[subQ2,1.0]])],"derivedFrom":subQ1}),1.0]])]});}
            var Q7;
            {var subQ0=sQuery(id+"F7.wireOp",EDGE,"E69");var subQ1=sQuery(id+"F7.wireOp",EDGE,"E61");var subQ2=makeQuery(id+"F7.imprint","INTERSECT",VERTEX,{"derivedFrom":[subQ1,subQ0]});Q7=makeQuery(id+"F7.imprint","IMPRINT",FACE,{"disambiguationData":[TD([[makeQuery(id+"F7.imprint","IMPRINT",EDGE,{"disambiguationData":[TD([[subQ2,-1.0]])],"derivedFrom":subQ1}),1.0]])]});}
            extrude(context, id + "F8", {"entities" : qUnion([Q0, Q1, Q2, Q3, Q4, Q5, Q6, Q7]), "depth" : 25.4 * mm});
        }
        {
            var Q0;
            Q0=makeQuery(id+"F8.opExtrude","SWEPT_FACE",FACE,{"disambiguationData":[OSD([sQuery(id+"F7.wireOp",EDGE,"E64")])]});
            var Q1;
            Q1=makeQuery(id+"F8.opExtrude","SWEPT_FACE",FACE,{"disambiguationData":[OSD([sQuery(id+"F7.wireOp",EDGE,"E62")])]});
            var Q2;
            Q2=makeQuery(id+"F8.opExtrude","SWEPT_FACE",FACE,{"disambiguationData":[OSD([sQuery(id+"F7.wireOp",EDGE,"E65")])]});
            var Q3;
            Q3=makeQuery(id+"F8.opExtrude","SWEPT_FACE",FACE,{"disambiguationData":[OSD([sQuery(id+"F7.wireOp",EDGE,"E60")])]});
            fillet(context, id + "F9", {"entities" : qUnion([Q0, Q1, Q2, Q3]), "radius" : 6.35 * mm, "tangentPropagation" : true, "allowEdgeOverflow" : false});
        }
        {
            var Q0;
            Q0=qCreatedBy(makeId("Front.planeOp"),FACE);
            var sketch = newSketch(context, id + "F10", { "sketchPlane" : qUnion([Q0])});
            skLineSegment(sketch, "E71", {"start": v(-382.56, 0) * mm, "end": v(382.56, 0) * mm});
            skLineSegment(sketch, "E72", {"start": v(382.56, 0) * mm, "end": v(0, 382.56) * mm});
            skLineSegment(sketch, "E73", {"start": v(0, 382.56) * mm, "end": v(-382.56, 0) * mm});
            skLineSegment(sketch, "E74.0", {"start": v(306.05, -76.51) * mm, "end": v(-76.51, 306.05) * mm});
            skLineSegment(sketch, "E75.0", {"start": v(229.54, -153.02) * mm, "end": v(-153.02, 229.54) * mm});
            skLineSegment(sketch, "E76.0", {"start": v(153.02, -229.54) * mm, "end": v(-229.54, 153.02) * mm});
            skLineSegment(sketch, "E77.0", {"start": v(0, -382.56) * mm, "end": v(-382.56, 0) * mm});
            skLineSegment(sketch, "E78", {"start": v(76.51, 0) * mm, "end": v(229.54, 153.02) * mm});
            skLineSegment(sketch, "E79", {"start": v(-76.51, 0) * mm, "end": v(153.02, 229.54) * mm});
            skLineSegment(sketch, "E80.0", {"start": v(76.51, -306.05) * mm, "end": v(-306.05, 76.51) * mm});
            skLineSegment(sketch, "E81", {"start": v(153.02, 229.54) * mm, "end": v(153.02, 76.51) * mm});
            skLineSegment(sketch, "E82", {"start": v(153.02, 76.51) * mm, "end": v(229.54, 153.02) * mm});
            skLineSegment(sketch, "E83", {"start": v(76.51, 153.02) * mm, "end": v(229.54, 153.02) * mm});
            skLineSegment(sketch, "E84", {"start": v(153.02, 153.02) * mm, "end": v(-38.26, 344.3) * mm});
            skLineSegment(sketch, "E85", {"start": v(-38.26, 344.3) * mm, "end": v(382.54, -76.49) * mm});
            skLineSegment(sketch, "E86.0", {"start": v(-114.77, 267.8) * mm, "end": v(306.02, -153) * mm});
            skLineSegment(sketch, "E87.0", {"start": v(-191.28, 191.28) * mm, "end": v(229.51, -229.51) * mm});
            skLineSegment(sketch, "E88.0", {"start": v(-267.8, 114.77) * mm, "end": v(153, -306.02) * mm});
            skLineSegment(sketch, "E89.0", {"start": v(-344.3, 38.26) * mm, "end": v(76.49, -382.54) * mm});
            skCircle(sketch, "E90", {"center": v(306.05, 0) * mm, "radius": 76.51 * mm});
            skCircle(sketch, "E91", {"center": v(153.02, 0) * mm, "radius": 76.51 * mm});
            skCircle(sketch, "E92", {"center": v(0, 0) * mm, "radius": 76.51 * mm});
            skCircle(sketch, "E93", {"center": v(-153.02, 0) * mm, "radius": 76.51 * mm});
            skCircle(sketch, "E94", {"center": v(-306.05, 0) * mm, "radius": 76.51 * mm});
            skLineSegment(sketch, "E95", {"start": v(306.05, 0) * mm, "end": v(306.05, -76.51) * mm});
            skLineSegment(sketch, "E96", {"start": v(153.02, 0) * mm, "end": v(153.02, -76.51) * mm});
            skLineSegment(sketch, "E97", {"start": v(0, 0) * mm, "end": v(0, -76.51) * mm});
            skLineSegment(sketch, "E98", {"start": v(-153.02, 0) * mm, "end": v(-153.02, -76.51) * mm});
            skLineSegment(sketch, "E99", {"start": v(-306.05, 0) * mm, "end": v(-306.05, -76.51) * mm});
            skSolve(sketch);
        }
        {
            var Q0;
            {var subQ0=sQuery(id+"F10.wireOp",EDGE,"E81");var subQ1=sQuery(id+"F10.wireOp",EDGE,"E72");var subQ2=makeQuery(id+"F10.imprint","INTERSECT",VERTEX,{"derivedFrom":[subQ1,sQuery(id+"F10.wireOp",EDGE,"E79"),subQ0]});Q0=makeQuery(id+"F10.imprint","IMPRINT",FACE,{"disambiguationData":[TD([[makeQuery(id+"F10.imprint","IMPRINT",EDGE,{"disambiguationData":[TD([[subQ2,1.0]])],"derivedFrom":subQ1}),1.0]])]});}
            var Q1;
            {var subQ0=sQuery(id+"F10.wireOp",EDGE,"E73");var subQ1=sQuery(id+"F10.wireOp",EDGE,"E72");var subQ2=makeQuery(id+"F10.imprint","INTERSECT",VERTEX,{"derivedFrom":[subQ1,subQ0]});Q1=makeQuery(id+"F10.imprint","IMPRINT",FACE,{"disambiguationData":[TD([[makeQuery(id+"F10.imprint","IMPRINT",EDGE,{"disambiguationData":[TD([[subQ2,-1.0]])],"derivedFrom":subQ0}),1.0]])]});}
            var Q2;
            {var subQ0=sQuery(id+"F10.wireOp",EDGE,"E91");var subQ1=sQuery(id+"F10.wireOp",EDGE,"E74.0");var subQ3=makeQuery(id+"F10.imprint","INTERSECT",VERTEX,{"derivedFrom":[sQuery(id+"F10.wireOp",EDGE,"E71"),subQ1,sQuery(id+"F10.wireOp",EDGE,"E90"),subQ0]});Q2=makeQuery(id+"F10.imprint","IMPRINT",FACE,{"disambiguationData":[TD([[makeQuery(id+"F10.imprint","IMPRINT",EDGE,{"disambiguationData":[TD([[subQ3,-1.0]])],"derivedFrom":subQ1}),-1.0]])]});}
            var Q3;
            {var subQ0=sQuery(id+"F10.wireOp",EDGE,"E92");var subQ1=sQuery(id+"F10.wireOp",EDGE,"E75.0");var subQ3=makeQuery(id+"F10.imprint","INTERSECT",VERTEX,{"derivedFrom":[subQ1,sQuery(id+"F10.wireOp",EDGE,"E79"),subQ0]});Q3=makeQuery(id+"F10.imprint","IMPRINT",FACE,{"disambiguationData":[TD([[makeQuery(id+"F10.imprint","IMPRINT",EDGE,{"disambiguationData":[TD([[subQ3,1.0]])],"derivedFrom":subQ1}),-1.0]])]});}
            var Q4;
            {var subQ0=sQuery(id+"F10.wireOp",EDGE,"E93");var subQ1=sQuery(id+"F10.wireOp",EDGE,"E76.0");var subQ3=makeQuery(id+"F10.imprint","INTERSECT",VERTEX,{"derivedFrom":[subQ1,subQ0]});Q4=makeQuery(id+"F10.imprint","IMPRINT",FACE,{"disambiguationData":[TD([[makeQuery(id+"F10.imprint","IMPRINT",EDGE,{"disambiguationData":[TD([[subQ3,1.0]])],"derivedFrom":subQ1}),-1.0]])]});}
            var Q5;
            {var subQ0=sQuery(id+"F10.wireOp",EDGE,"E94");var subQ1=sQuery(id+"F10.wireOp",EDGE,"E80.0");var subQ2=makeQuery(id+"F10.imprint","INTERSECT",VERTEX,{"derivedFrom":[sQuery(id+"F10.wireOp",EDGE,"E73"),subQ1,subQ0]});Q5=makeQuery(id+"F10.imprint","IMPRINT",FACE,{"disambiguationData":[TD([[makeQuery(id+"F10.imprint","IMPRINT",EDGE,{"disambiguationData":[TD([[subQ2,1.0]])],"derivedFrom":subQ1}),-1.0]])]});}
            var Q6;
            {var subQ0=sQuery(id+"F10.wireOp",EDGE,"E73");var subQ3=sQuery(id+"F10.wireOp",EDGE,"E89.0");var subQ5=makeQuery(id+"F10.imprint","INTERSECT",VERTEX,{"derivedFrom":[subQ0,subQ3]});Q6=makeQuery(id+"F10.imprint","IMPRINT",FACE,{"disambiguationData":[TD([[makeQuery(id+"F10.imprint","IMPRINT",EDGE,{"disambiguationData":[TD([[subQ5,-1.0]])],"derivedFrom":subQ3}),-1.0]])]});}
            var Q7;
            {var subQ4=sQuery(id+"F10.wireOp",EDGE,"E99");Q7=makeQuery(id+"F10.imprint","IMPRINT",FACE,{"disambiguationData":[TD([[makeQuery(id+"F10.imprint","IMPRINT",EDGE,{"derivedFrom":subQ4}),-1.0]])]});}
            var Q8;
            {var subQ0=sQuery(id+"F10.wireOp",EDGE,"E98");Q8=makeQuery(id+"F10.imprint","IMPRINT",FACE,{"disambiguationData":[TD([[makeQuery(id+"F10.imprint","IMPRINT",EDGE,{"derivedFrom":subQ0}),-1.0]])]});}
            var Q9;
            {var subQ0=sQuery(id+"F10.wireOp",EDGE,"E88.0");var subQ3=sQuery(id+"F10.wireOp",EDGE,"E93");var subQ5=makeQuery(id+"F10.imprint","INTERSECT",VERTEX,{"disambiguationData":[OD(1.0)],"derivedFrom":[subQ0,subQ3]});Q9=makeQuery(id+"F10.imprint","IMPRINT",FACE,{"disambiguationData":[TD([[makeQuery(id+"F10.imprint","IMPRINT",EDGE,{"disambiguationData":[TD([[subQ5,-1.0]])],"derivedFrom":subQ0}),-1.0]])]});}
            var Q10;
            {var subQ4=sQuery(id+"F10.wireOp",EDGE,"E97");Q10=makeQuery(id+"F10.imprint","IMPRINT",FACE,{"disambiguationData":[TD([[makeQuery(id+"F10.imprint","IMPRINT",EDGE,{"derivedFrom":subQ4}),-1.0]])]});}
            var Q11;
            {var subQ0=sQuery(id+"F10.wireOp",EDGE,"E79");var subQ3=sQuery(id+"F10.wireOp",EDGE,"E87.0");var subQ5=makeQuery(id+"F10.imprint","INTERSECT",VERTEX,{"derivedFrom":[subQ0,subQ3]});Q11=makeQuery(id+"F10.imprint","IMPRINT",FACE,{"disambiguationData":[TD([[makeQuery(id+"F10.imprint","IMPRINT",EDGE,{"disambiguationData":[TD([[subQ5,-1.0]])],"derivedFrom":subQ3}),-1.0]])]});}
            var Q12;
            {var subQ4=sQuery(id+"F10.wireOp",EDGE,"E96");Q12=makeQuery(id+"F10.imprint","IMPRINT",FACE,{"disambiguationData":[TD([[makeQuery(id+"F10.imprint","IMPRINT",EDGE,{"derivedFrom":subQ4}),-1.0]])]});}
            var Q13;
            {var subQ0=sQuery(id+"F10.wireOp",EDGE,"E78");var subQ3=sQuery(id+"F10.wireOp",EDGE,"E86.0");var subQ5=makeQuery(id+"F10.imprint","INTERSECT",VERTEX,{"derivedFrom":[subQ0,subQ3]});Q13=makeQuery(id+"F10.imprint","IMPRINT",FACE,{"disambiguationData":[TD([[makeQuery(id+"F10.imprint","IMPRINT",EDGE,{"disambiguationData":[TD([[subQ5,-1.0]])],"derivedFrom":subQ3}),-1.0]])]});}
            var Q14;
            {var subQ0=sQuery(id+"F10.wireOp",EDGE,"E95");Q14=makeQuery(id+"F10.imprint","IMPRINT",FACE,{"disambiguationData":[TD([[makeQuery(id+"F10.imprint","IMPRINT",EDGE,{"derivedFrom":subQ0}),-1.0]])]});}
            var Q15;
            {var subQ0=sQuery(id+"F10.wireOp",EDGE,"E85");var subQ3=sQuery(id+"F10.wireOp",EDGE,"E90");var subQ5=makeQuery(id+"F10.imprint","INTERSECT",VERTEX,{"disambiguationData":[OD(1.0)],"derivedFrom":[subQ0,subQ3]});Q15=makeQuery(id+"F10.imprint","IMPRINT",FACE,{"disambiguationData":[TD([[makeQuery(id+"F10.imprint","IMPRINT",EDGE,{"disambiguationData":[TD([[subQ5,-1.0]])],"derivedFrom":subQ0}),-1.0]])]});}
            var Q16;
            {var subQ0=sQuery(id+"F10.wireOp",EDGE,"E82");var subQ5=sQuery(id+"F10.wireOp",EDGE,"E85");var subQ6=makeQuery(id+"F10.imprint","INTERSECT",VERTEX,{"derivedFrom":[subQ0,subQ5]});Q16=makeQuery(id+"F10.imprint","IMPRINT",FACE,{"disambiguationData":[TD([[makeQuery(id+"F10.imprint","IMPRINT",EDGE,{"disambiguationData":[TD([[subQ6,-1.0]])],"derivedFrom":subQ5}),1.0]])]});}
            var Q17;
            {var subQ0=sQuery(id+"F10.wireOp",EDGE,"E74.0");var subQ1=sQuery(id+"F10.wireOp",EDGE,"E73");var subQ2=makeQuery(id+"F10.imprint","INTERSECT",VERTEX,{"derivedFrom":[subQ1,subQ0]});Q17=makeQuery(id+"F10.imprint","IMPRINT",FACE,{"disambiguationData":[TD([[makeQuery(id+"F10.imprint","IMPRINT",EDGE,{"disambiguationData":[TD([[subQ2,1.0]])],"derivedFrom":subQ1}),1.0]])]});}
            var Q18;
            {var subQ0=sQuery(id+"F10.wireOp",EDGE,"E74.0");var subQ1=sQuery(id+"F10.wireOp",EDGE,"E73");var subQ2=makeQuery(id+"F10.imprint","INTERSECT",VERTEX,{"derivedFrom":[subQ1,subQ0]});Q18=makeQuery(id+"F10.imprint","IMPRINT",FACE,{"disambiguationData":[TD([[makeQuery(id+"F10.imprint","IMPRINT",EDGE,{"disambiguationData":[TD([[subQ2,-1.0]])],"derivedFrom":subQ1}),1.0]])]});}
            var Q19;
            {var subQ0=sQuery(id+"F10.wireOp",EDGE,"E75.0");var subQ1=sQuery(id+"F10.wireOp",EDGE,"E73");var subQ2=makeQuery(id+"F10.imprint","INTERSECT",VERTEX,{"derivedFrom":[subQ1,subQ0]});Q19=makeQuery(id+"F10.imprint","IMPRINT",FACE,{"disambiguationData":[TD([[makeQuery(id+"F10.imprint","IMPRINT",EDGE,{"disambiguationData":[TD([[subQ2,1.0]])],"derivedFrom":subQ1}),1.0]])]});}
            var Q20;
            {var subQ0=sQuery(id+"F10.wireOp",EDGE,"E75.0");var subQ1=sQuery(id+"F10.wireOp",EDGE,"E73");var subQ2=makeQuery(id+"F10.imprint","INTERSECT",VERTEX,{"derivedFrom":[subQ1,subQ0]});Q20=makeQuery(id+"F10.imprint","IMPRINT",FACE,{"disambiguationData":[TD([[makeQuery(id+"F10.imprint","IMPRINT",EDGE,{"disambiguationData":[TD([[subQ2,-1.0]])],"derivedFrom":subQ1}),1.0]])]});}
            var Q21;
            {var subQ0=sQuery(id+"F10.wireOp",EDGE,"E76.0");var subQ1=sQuery(id+"F10.wireOp",EDGE,"E73");var subQ2=makeQuery(id+"F10.imprint","INTERSECT",VERTEX,{"derivedFrom":[subQ1,subQ0]});Q21=makeQuery(id+"F10.imprint","IMPRINT",FACE,{"disambiguationData":[TD([[makeQuery(id+"F10.imprint","IMPRINT",EDGE,{"disambiguationData":[TD([[subQ2,-1.0]])],"derivedFrom":subQ1}),1.0]])]});}
            var Q22;
            {var subQ2=sQuery(id+"F10.wireOp",EDGE,"E73");var subQ4=sQuery(id+"F10.wireOp",EDGE,"E88.0");var subQ5=makeQuery(id+"F10.imprint","INTERSECT",VERTEX,{"derivedFrom":[subQ2,subQ4]});Q22=makeQuery(id+"F10.imprint","IMPRINT",FACE,{"disambiguationData":[TD([[makeQuery(id+"F10.imprint","IMPRINT",EDGE,{"disambiguationData":[TD([[subQ5,-1.0]])],"derivedFrom":subQ4}),-1.0]])]});}
            var Q23;
            {var subQ1=sQuery(id+"F10.wireOp",EDGE,"E78");var subQ3=sQuery(id+"F10.wireOp",EDGE,"E86.0");var subQ4=makeQuery(id+"F10.imprint","INTERSECT",VERTEX,{"derivedFrom":[subQ1,subQ3]});Q23=makeQuery(id+"F10.imprint","IMPRINT",FACE,{"disambiguationData":[TD([[makeQuery(id+"F10.imprint","IMPRINT",EDGE,{"disambiguationData":[TD([[subQ4,1.0]])],"derivedFrom":subQ3}),-1.0]])]});}
            var Q24;
            {var subQ1=sQuery(id+"F10.wireOp",EDGE,"E79");var subQ3=sQuery(id+"F10.wireOp",EDGE,"E87.0");var subQ4=makeQuery(id+"F10.imprint","INTERSECT",VERTEX,{"derivedFrom":[subQ1,subQ3]});Q24=makeQuery(id+"F10.imprint","IMPRINT",FACE,{"disambiguationData":[TD([[makeQuery(id+"F10.imprint","IMPRINT",EDGE,{"disambiguationData":[TD([[subQ4,1.0]])],"derivedFrom":subQ3}),-1.0]])]});}
            var Q25;
            {var subQ1=sQuery(id+"F10.wireOp",EDGE,"E79");var subQ3=sQuery(id+"F10.wireOp",EDGE,"E85");var subQ4=makeQuery(id+"F10.imprint","INTERSECT",VERTEX,{"derivedFrom":[subQ1,subQ3]});Q25=makeQuery(id+"F10.imprint","IMPRINT",FACE,{"disambiguationData":[TD([[makeQuery(id+"F10.imprint","IMPRINT",EDGE,{"disambiguationData":[TD([[subQ4,-1.0]])],"derivedFrom":subQ1}),-1.0]])]});}
            var Q26;
            {var subQ1=sQuery(id+"F10.wireOp",EDGE,"E82");var subQ3=sQuery(id+"F10.wireOp",EDGE,"E85");var subQ4=makeQuery(id+"F10.imprint","INTERSECT",VERTEX,{"derivedFrom":[subQ1,subQ3]});Q26=makeQuery(id+"F10.imprint","IMPRINT",FACE,{"disambiguationData":[TD([[makeQuery(id+"F10.imprint","IMPRINT",EDGE,{"disambiguationData":[TD([[subQ4,-1.0]])],"derivedFrom":subQ1}),1.0]])]});}
            var Q27;
            {var subQ0=sQuery(id+"F10.wireOp",EDGE,"E89.0");var subQ6=sQuery(id+"F10.wireOp",EDGE,"E73");var subQ8=makeQuery(id+"F10.imprint","INTERSECT",VERTEX,{"derivedFrom":[subQ6,subQ0]});Q27=makeQuery(id+"F10.imprint","IMPRINT",FACE,{"disambiguationData":[TD([[makeQuery(id+"F10.imprint","IMPRINT",EDGE,{"disambiguationData":[TD([[subQ8,1.0]])],"derivedFrom":subQ6}),1.0]])]});}
            var Q28;
            {var subQ0=sQuery(id+"F10.wireOp",EDGE,"E93");var subQ1=sQuery(id+"F10.wireOp",EDGE,"E76.0");var subQ6=makeQuery(id+"F10.imprint","INTERSECT",VERTEX,{"derivedFrom":[subQ1,subQ0]});Q28=makeQuery(id+"F10.imprint","IMPRINT",FACE,{"disambiguationData":[TD([[makeQuery(id+"F10.imprint","IMPRINT",EDGE,{"disambiguationData":[TD([[subQ6,-1.0]])],"derivedFrom":subQ0}),1.0]])]});}
            var Q29;
            {var subQ4=sQuery(id+"F10.wireOp",EDGE,"E87.0");var subQ6=sQuery(id+"F10.wireOp",EDGE,"E79");var subQ8=makeQuery(id+"F10.imprint","INTERSECT",VERTEX,{"derivedFrom":[subQ6,subQ4]});Q29=makeQuery(id+"F10.imprint","IMPRINT",FACE,{"disambiguationData":[TD([[makeQuery(id+"F10.imprint","IMPRINT",EDGE,{"disambiguationData":[TD([[subQ8,-1.0]])],"derivedFrom":subQ6}),-1.0]])]});}
            var Q30;
            {var subQ0=sQuery(id+"F10.wireOp",EDGE,"E86.0");var subQ6=sQuery(id+"F10.wireOp",EDGE,"E78");var subQ8=makeQuery(id+"F10.imprint","INTERSECT",VERTEX,{"derivedFrom":[subQ6,subQ0]});Q30=makeQuery(id+"F10.imprint","IMPRINT",FACE,{"disambiguationData":[TD([[makeQuery(id+"F10.imprint","IMPRINT",EDGE,{"disambiguationData":[TD([[subQ8,-1.0]])],"derivedFrom":subQ0}),1.0]])]});}
            var Q31;
            {var subQ0=sQuery(id+"F10.wireOp",EDGE,"E90");var subQ1=sQuery(id+"F10.wireOp",EDGE,"E72");var subQ6=makeQuery(id+"F10.imprint","INTERSECT",VERTEX,{"derivedFrom":[subQ1,subQ0]});Q31=makeQuery(id+"F10.imprint","IMPRINT",FACE,{"disambiguationData":[TD([[makeQuery(id+"F10.imprint","IMPRINT",EDGE,{"disambiguationData":[TD([[subQ6,-1.0]])],"derivedFrom":subQ0}),1.0]])]});}
            var Q32;
            {var subQ2=sQuery(id+"F10.wireOp",EDGE,"E76.0");var subQ6=sQuery(id+"F10.wireOp",EDGE,"E73");var subQ7=makeQuery(id+"F10.imprint","INTERSECT",VERTEX,{"derivedFrom":[subQ6,subQ2]});Q32=makeQuery(id+"F10.imprint","IMPRINT",FACE,{"disambiguationData":[TD([[makeQuery(id+"F10.imprint","IMPRINT",EDGE,{"disambiguationData":[TD([[subQ7,1.0]])],"derivedFrom":subQ6}),1.0]])]});}
            var Q33;
            {var subQ0=sQuery(id+"F10.wireOp",EDGE,"E86.0");var subQ1=sQuery(id+"F10.wireOp",EDGE,"E79");var subQ2=makeQuery(id+"F10.imprint","INTERSECT",VERTEX,{"derivedFrom":[subQ1,subQ0]});Q33=makeQuery(id+"F10.imprint","IMPRINT",FACE,{"disambiguationData":[TD([[makeQuery(id+"F10.imprint","IMPRINT",EDGE,{"disambiguationData":[TD([[subQ2,-1.0]])],"derivedFrom":subQ0}),-1.0]])]});}
            var Q34;
            {var subQ1=sQuery(id+"F10.wireOp",EDGE,"E82");var subQ4=sQuery(id+"F10.wireOp",EDGE,"E85");var subQ5=makeQuery(id+"F10.imprint","INTERSECT",VERTEX,{"derivedFrom":[subQ1,subQ4]});Q34=makeQuery(id+"F10.imprint","IMPRINT",FACE,{"disambiguationData":[TD([[makeQuery(id+"F10.imprint","IMPRINT",EDGE,{"disambiguationData":[TD([[subQ5,-1.0]])],"derivedFrom":subQ4}),-1.0]])]});}
            var Q35;
            {var subQ1=sQuery(id+"F10.wireOp",EDGE,"E74.0");var subQ3=sQuery(id+"F10.wireOp",EDGE,"E83");var subQ4=makeQuery(id+"F10.imprint","INTERSECT",VERTEX,{"derivedFrom":[subQ1,sQuery(id+"F10.wireOp",EDGE,"E79"),subQ3]});Q35=makeQuery(id+"F10.imprint","IMPRINT",FACE,{"disambiguationData":[TD([[makeQuery(id+"F10.imprint","IMPRINT",EDGE,{"disambiguationData":[TD([[subQ4,-1.0]])],"derivedFrom":subQ3}),-1.0]])]});}
            var Q36;
            {var subQ3=sQuery(id+"F10.wireOp",EDGE,"E79");var subQ5=sQuery(id+"F10.wireOp",EDGE,"E86.0");var subQ6=makeQuery(id+"F10.imprint","INTERSECT",VERTEX,{"derivedFrom":[subQ3,subQ5]});Q36=makeQuery(id+"F10.imprint","IMPRINT",FACE,{"disambiguationData":[TD([[makeQuery(id+"F10.imprint","IMPRINT",EDGE,{"disambiguationData":[TD([[subQ6,-1.0]])],"derivedFrom":subQ5}),1.0]])]});}
            var Q37;
            {var subQ0=sQuery(id+"F10.wireOp",EDGE,"E87.0");var subQ1=sQuery(id+"F10.wireOp",EDGE,"E79");var subQ2=makeQuery(id+"F10.imprint","INTERSECT",VERTEX,{"derivedFrom":[subQ1,subQ0]});Q37=makeQuery(id+"F10.imprint","IMPRINT",FACE,{"disambiguationData":[TD([[makeQuery(id+"F10.imprint","IMPRINT",EDGE,{"disambiguationData":[TD([[subQ2,1.0]])],"derivedFrom":subQ0}),1.0]])]});}
            var Q38;
            {var subQ1=sQuery(id+"F10.wireOp",EDGE,"E79");var subQ3=sQuery(id+"F10.wireOp",EDGE,"E85");var subQ4=makeQuery(id+"F10.imprint","INTERSECT",VERTEX,{"derivedFrom":[subQ1,subQ3]});Q38=makeQuery(id+"F10.imprint","IMPRINT",FACE,{"disambiguationData":[TD([[makeQuery(id+"F10.imprint","IMPRINT",EDGE,{"disambiguationData":[TD([[subQ4,1.0]])],"derivedFrom":subQ1}),-1.0]])]});}
            var Q39;
            {var subQ0=sQuery(id+"F10.wireOp",EDGE,"E82");var subQ3=sQuery(id+"F10.wireOp",EDGE,"E85");var subQ5=makeQuery(id+"F10.imprint","INTERSECT",VERTEX,{"derivedFrom":[subQ0,subQ3]});Q39=makeQuery(id+"F10.imprint","IMPRINT",FACE,{"disambiguationData":[TD([[makeQuery(id+"F10.imprint","IMPRINT",EDGE,{"disambiguationData":[TD([[subQ5,1.0]])],"derivedFrom":subQ3}),-1.0]])]});}
            var Q40;
            {var subQ1=sQuery(id+"F10.wireOp",EDGE,"E78");var subQ3=sQuery(id+"F10.wireOp",EDGE,"E86.0");var subQ4=makeQuery(id+"F10.imprint","INTERSECT",VERTEX,{"derivedFrom":[subQ1,subQ3]});Q40=makeQuery(id+"F10.imprint","IMPRINT",FACE,{"disambiguationData":[TD([[makeQuery(id+"F10.imprint","IMPRINT",EDGE,{"disambiguationData":[TD([[subQ4,1.0]])],"derivedFrom":subQ3}),1.0]])]});}
            extrude(context, id + "F11", {"entities" : qUnion([Q0, Q1, Q2, Q3, Q4, Q5, Q6, Q7, Q8, Q9, Q10, Q11, Q12, Q13, Q14, Q15, Q16, Q17, Q18, Q19, Q20, Q21, Q22, Q23, Q24, Q25, Q26, Q27, Q28, Q29, Q30, Q31, Q32, Q33, Q34, Q35, Q36, Q37, Q38, Q39, Q40]), "depth" : 25.4 * mm});
        }
        {
            var Q0;
            {var subQ0=sQuery(id+"F10.wireOp",EDGE,"E95");Q0=makeQuery(id+"F10.imprint","IMPRINT",FACE,{"disambiguationData":[TD([[makeQuery(id+"F10.imprint","IMPRINT",EDGE,{"derivedFrom":subQ0}),-1.0]])]});}
            var Q1;
            {var subQ0=sQuery(id+"F10.wireOp",EDGE,"E90");var subQ1=sQuery(id+"F10.wireOp",EDGE,"E72");var subQ6=makeQuery(id+"F10.imprint","INTERSECT",VERTEX,{"derivedFrom":[subQ1,subQ0]});Q1=makeQuery(id+"F10.imprint","IMPRINT",FACE,{"disambiguationData":[TD([[makeQuery(id+"F10.imprint","IMPRINT",EDGE,{"disambiguationData":[TD([[subQ6,-1.0]])],"derivedFrom":subQ0}),1.0]])]});}
            var Q2;
            {var subQ0=sQuery(id+"F10.wireOp",EDGE,"E85");var subQ3=sQuery(id+"F10.wireOp",EDGE,"E90");var subQ5=makeQuery(id+"F10.imprint","INTERSECT",VERTEX,{"disambiguationData":[OD(1.0)],"derivedFrom":[subQ0,subQ3]});Q2=makeQuery(id+"F10.imprint","IMPRINT",FACE,{"disambiguationData":[TD([[makeQuery(id+"F10.imprint","IMPRINT",EDGE,{"disambiguationData":[TD([[subQ5,-1.0]])],"derivedFrom":subQ0}),-1.0]])]});}
            extrude(context, id + "F12", {"entities" : qUnion([Q0, Q1, Q2]), "depth" : 142.24 * mm});
        }
        {
            var Q0;
            Q0=makeQuery(id+"F12.opExtrude","SWEPT_EDGE",EDGE,{"disambiguationData":[OSD([sQuery(id+"F10.wireOp",EDGE,"E71"),sQuery(id+"F10.wireOp",EDGE,"E72"),sQuery(id+"F10.wireOp",EDGE,"E90")])]});
            var Q1;
            Q1=makeQuery(id+"F12.opExtrude","SWEPT_EDGE",EDGE,{"disambiguationData":[OSD([sQuery(id+"F10.wireOp",EDGE,"E74.0"),sQuery(id+"F10.wireOp",EDGE,"E90"),sQuery(id+"F10.wireOp",EDGE,"E95")])]});
            fillet(context, id + "F13", {"entities" : qUnion([Q0, Q1]), "radius" : 5.08 * mm, "tangentPropagation" : true, "allowEdgeOverflow" : false});
        }
    });
